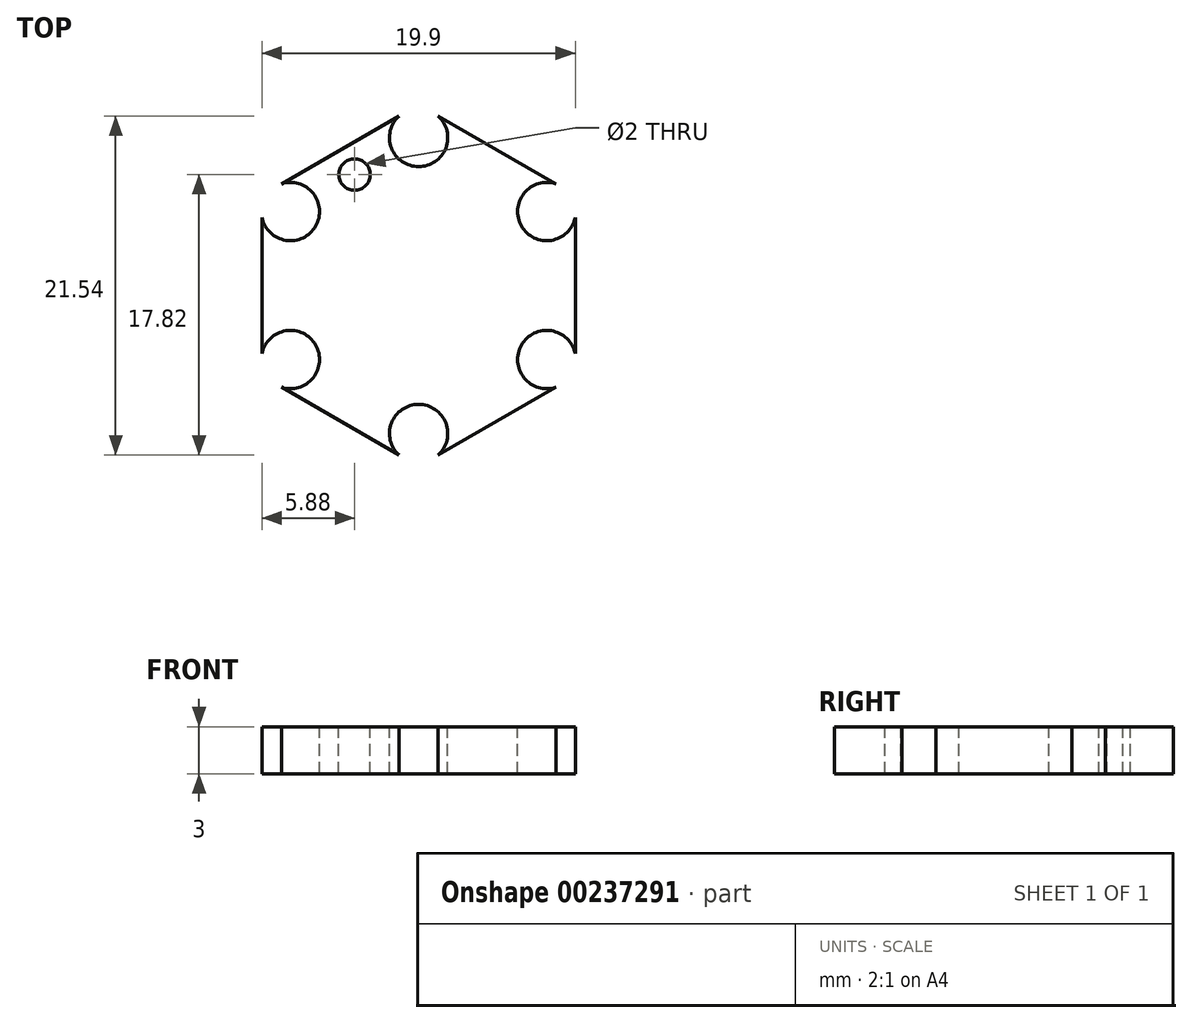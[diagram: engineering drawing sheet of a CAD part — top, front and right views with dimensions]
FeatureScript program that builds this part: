
annotation { "Feature Type Name" : "Feature", "Feature Type Description" : "" }
export const myFeature = defineFeature(function(context is Context, id is Id, definition is map)
    precondition{}
    {
        {
            var Q0;
            Q0=qCreatedBy(makeId("Top.planeOp"),FACE);
            var sketch = newSketch(context, id + "F0", { "sketchPlane" : qUnion([Q0])});
            skCircle(sketch, "E0.cCircle", {"center": v(0, 0) * mm, "radius": 9.95 * mm, "construction": true});
            skLineSegment(sketch, "E0.0", {"start": v(9.95, 4.31) * mm, "end": v(9.95, -4.31) * mm});
            skLineSegment(sketch, "E0.1", {"start": v(8.71, -6.46) * mm, "end": v(1.24, -10.77) * mm});
            skLineSegment(sketch, "E0.3", {"start": v(-9.95, -4.31) * mm, "end": v(-9.95, 4.31) * mm});
            skLineSegment(sketch, "E0.4", {"start": v(-8.71, 6.46) * mm, "end": v(-1.24, 10.77) * mm});
            skLineSegment(sketch, "E0.5", {"start": v(1.24, 10.77) * mm, "end": v(8.71, 6.46) * mm});
            skPoint(sketch, "E0.0.midPoint", {"position": v(9.95, 0) * mm});
            skCircle(sketch, "E1", {"center": v(0, 0) * mm, "radius": 7.55 * mm, "construction": true});
            skLineSegment(sketch, "E2", {"start": v(0, 0) * mm, "end": v(9.95, -5.74) * mm, "construction": true});
            skArc(sketch, "E3", {"start": v(9.95, -4.31) * mm, "mid": v(6.54, -3.78) * mm, "end": v(8.71, -6.46) * mm});
            skArc(sketch, "E4.1.0", {"start": v(8.71, 6.46) * mm, "mid": v(6.54, 3.78) * mm, "end": v(9.95, 4.31) * mm});
            skArc(sketch, "E4.2.0", {"start": v(-1.24, 10.77) * mm, "mid": v(0, 7.55) * mm, "end": v(1.24, 10.77) * mm});
            skArc(sketch, "E4.3.0", {"start": v(-9.95, 4.31) * mm, "mid": v(-6.54, 3.77) * mm, "end": v(-8.71, 6.46) * mm});
            skArc(sketch, "E4.4.0", {"start": v(-8.71, -6.46) * mm, "mid": v(-6.54, -3.78) * mm, "end": v(-9.95, -4.31) * mm});
            skArc(sketch, "E4.5.0", {"start": v(1.24, -10.77) * mm, "mid": v(0, -7.55) * mm, "end": v(-1.24, -10.77) * mm});
            skPoint(sketch, "E5.orphan", {"position": v(-9.95, 5.74) * mm});
            skPoint(sketch, "E6.orphan", {"position": v(-9.95, -5.74) * mm});
            skLineSegment(sketch, "E7.trimOffspring", {"start": v(-1.24, -10.77) * mm, "end": v(-8.71, -6.46) * mm});
            skPoint(sketch, "E8.orphan", {"position": v(9.95, 5.74) * mm});
            skPoint(sketch, "E9.orphan", {"position": v(0, 11.49) * mm});
            skCircle(sketch, "E10", {"center": v(4.07, -7.05) * mm, "radius": 1 * mm});
            skLineSegment(sketch, "E11", {"start": v(-8.14, -4.7) * mm, "end": v(8.14, 4.7) * mm, "construction": true});
            skCircle(sketch, "E12.MirrorC", {"center": v(-4.07, 7.05) * mm, "radius": 1 * mm});
            skSolve(sketch);
        }
        {
            var Q0;
            Q0=makeQuery(id+"F0.imprint","IMPRINT",FACE,{"disambiguationData":[TD([[makeQuery(id+"F0.imprint","IMPRINT",EDGE,{"derivedFrom":sQuery(id+"F0.wireOp",EDGE,"E0.0")}),-1.0]])]});
            var Q1;
            Q1=makeQuery(id+"F0.imprint","IMPRINT",FACE,{"disambiguationData":[TD([[makeQuery(id+"F0.imprint","IMPRINT",EDGE,{"derivedFrom":sQuery(id+"F0.wireOp",EDGE,"E10")}),1.0]])]});
            var Q2;
            Q2=makeQuery(id+"F0.imprint","IMPRINT",FACE,{"disambiguationData":[TD([[makeQuery(id+"F0.imprint","IMPRINT",EDGE,{"derivedFrom":sQuery(id+"F0.wireOp",EDGE,"E12.MirrorC")}),-1.0]])]});
            extrude(context, id + "F1", {"entities" : qUnion([Q0, Q1, Q2]), "oppositeDirection" : true, "depth" : 1.5 * mm});
        }
        {
            var Q0;
            Q0=makeQuery(id+"F1.opExtrude","CAP_FACE",FACE,{"disambiguationData":[OSD([sQuery(id+"F0.wireOp",EDGE,"E0.0"),sQuery(id+"F0.wireOp",EDGE,"E0.1"),sQuery(id+"F0.wireOp",EDGE,"E0.3"),sQuery(id+"F0.wireOp",EDGE,"E0.4"),sQuery(id+"F0.wireOp",EDGE,"E0.5"),sQuery(id+"F0.wireOp",EDGE,"E3"),sQuery(id+"F0.wireOp",EDGE,"E4.1.0"),sQuery(id+"F0.wireOp",EDGE,"E4.2.0"),sQuery(id+"F0.wireOp",EDGE,"E4.3.0"),sQuery(id+"F0.wireOp",EDGE,"E4.4.0"),sQuery(id+"F0.wireOp",EDGE,"E4.5.0"),sQuery(id+"F0.wireOp",EDGE,"E7.trimOffspring")])],"isStart":true});
            var sketch = newSketch(context, id + "F2", { "sketchPlane" : qUnion([Q0])});
            skCircle(sketch, "E13", {"center": v(0, 0) * mm, "radius": 4 * mm});
            skSolve(sketch);
        }
        {
            var Q0;
            Q0=makeQuery(id+"F2.imprint","IMPRINT",FACE,{"disambiguationData":[TD([[makeQuery(id+"F2.imprint","IMPRINT",EDGE,{"derivedFrom":sQuery(id+"F2.wireOp",EDGE,"E13")}),1.0]])]});
            var Q1;
            Q1=makeQuery(id+"F0.imprint","IMPRINT",FACE,{"disambiguationData":[TD([[makeQuery(id+"F0.imprint","IMPRINT",EDGE,{"derivedFrom":sQuery(id+"F0.wireOp",EDGE,"E12.MirrorC")}),-1.0]])]});
            var Q2;
            Q2=makeQuery(id+"F0.imprint","IMPRINT",FACE,{"disambiguationData":[TD([[makeQuery(id+"F0.imprint","IMPRINT",EDGE,{"derivedFrom":sQuery(id+"F0.wireOp",EDGE,"E10")}),1.0]])]});
            extrude(context, id + "F3", {"entities" : qUnion([Q0, Q1, Q2]), "operationType" : NewBodyOperationType.ADD, "depth" : 1.5 * mm});
        }
    });
